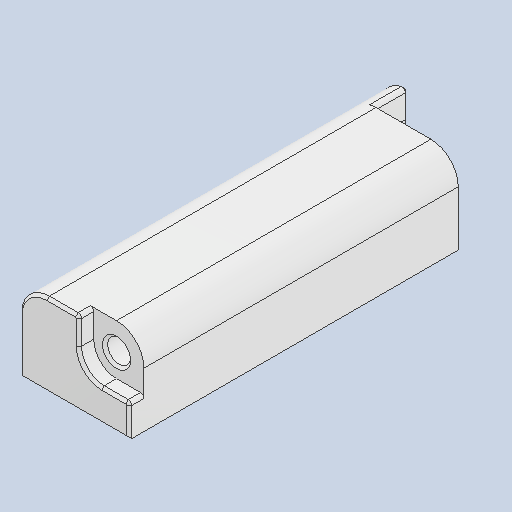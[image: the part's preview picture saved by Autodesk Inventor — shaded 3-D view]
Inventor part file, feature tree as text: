
AUTODESK INVENTOR PART (.ipt)
format: ipt  version: 2023.3 (Build 273359000, 359)  size: 198,144 bytes
history: native  units: mm
features: fillet x5, sketch x5, extrude x4, chamfer x2, hole x1
ambient origin geometry x8: Origin, YZ Plane, XZ Plane, XY Plane, X Axis, Y Axis, Z Axis, Center Point
bodies: Solid1 (feature_tree)
feature tree (17):
  extrude  "Extrusion1"  Depth=25.4mm
  extrude  "Extrusion2"  Depth=11.621mm
  extrude  "Extrusion3"  Depth=3.429mm TaperAngle=0.0deg
  hole  "Hole1"  [1 undecoded]
  fillet  "Fillet1"  Radius=7.938mm
  fillet  "Fillet2"  Radius=6.35mm
  fillet  "Fillet3"  Radius=6.35mm
  fillet  "Fillet4"  Radius=6.35mm
  chamfer  "Chamfer1"  Distance=0.794mm
  extrude  "Extrusion4"  Depth=5.271mm
  fillet  "Fillet5"  Radius=13.208mm
  chamfer  "Chamfer2"  Distance=0.6mm Angle=45.0deg
  sketch  "Sketch1"  dims[d0=25.4mm d1=25.4mm]
  sketch  "Sketch2"  dims[d2=84.138mm d3=0.0mm d4=11.621mm]
  sketch  "Sketch3"  dims[d5=11.621mm d6=3.429mm d7=0.0mm]
  sketch  "Sketch4"  dims[d8=19.558mm d9=19.558mm d10=7.938mm d11=0.0mm d12=6.35mm d13=6.35mm]
  sketch  "Sketch5"  dims[d14=5.334mm d15=6.0mm d16=9.779mm d17=2.0mm d18=14.3117mm d19=8.0mm d20=20.594885mm d21=6.35mm d22=0.794mm d23=5.271mm d24=13.208mm d25=0.6mm d26=2.0mm d27=45.0deg d28=6.35mm d29=25.4mm d30=84.138mm d31=0.0mm d32=0.794mm d33=0.6mm d34=2.0mm d35=45.0deg]
note: 1 required parameter value undecoded (feature->parameter linkage not recoverable at this tier; creation-order binding heuristic only, values carry confidence <= 0.55)
